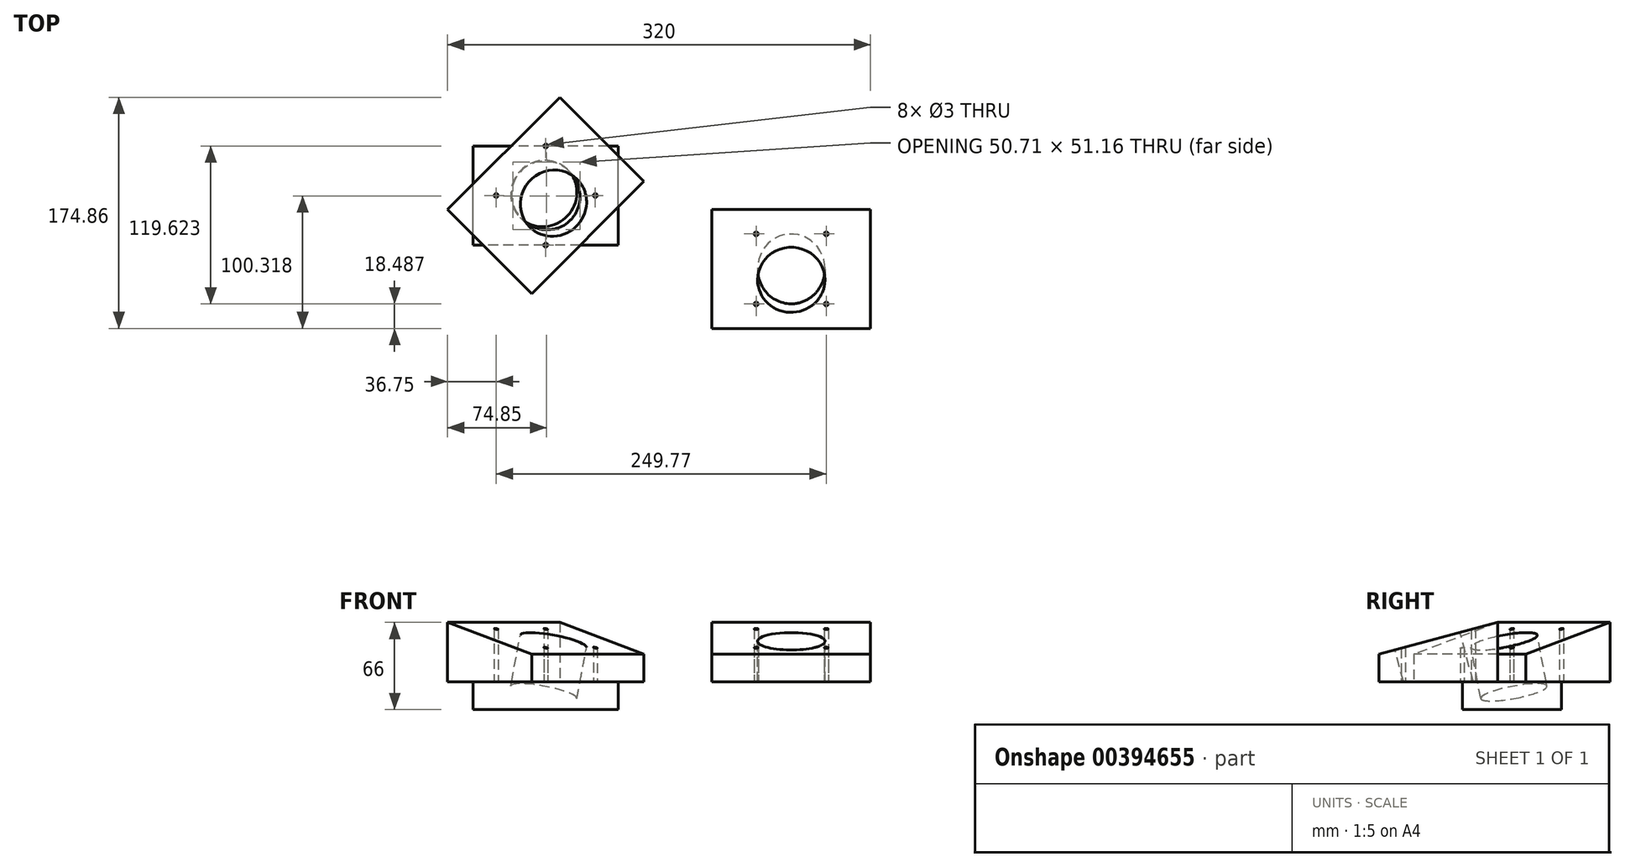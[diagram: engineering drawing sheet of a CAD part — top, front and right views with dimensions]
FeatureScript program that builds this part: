
annotation { "Feature Type Name" : "Feature", "Feature Type Description" : "" }
export const myFeature = defineFeature(function(context is Context, id is Id, definition is map)
    precondition{}
    {
        {
            var Q0;
            Q0=qCreatedBy(makeId("Top.planeOp"),FACE);
            var sketch = newSketch(context, id + "F0", { "sketchPlane" : qUnion([Q0])});
            skLineSegment(sketch, "E0.bottom", {"start": v(55, -37.5) * mm, "end": v(-55, -37.5) * mm});
            skLineSegment(sketch, "E0.top", {"start": v(55, 37.5) * mm, "end": v(-55, 37.5) * mm});
            skLineSegment(sketch, "E0.left", {"start": v(55, -37.5) * mm, "end": v(55, 37.5) * mm});
            skLineSegment(sketch, "E0.right", {"start": v(-55, -37.5) * mm, "end": v(-55, 37.5) * mm});
            skPoint(sketch, "E0.middle", {"position": v(0, 0) * mm});
            skSolve(sketch);
        }
        {
            var Q0;
            Q0=makeQuery(id+"F0.imprint","IMPRINT",FACE,{"disambiguationData":[TD([[makeQuery(id+"F0.imprint","IMPRINT",EDGE,{"derivedFrom":sQuery(id+"F0.wireOp",EDGE,"E0.bottom")}),-1.0]])]});
            extrude(context, id + "F1", {"entities" : qUnion([Q0]), "depth" : 21 * mm, "offsetDistance" : 25 * mm});
        }
        {
            var Q0;
            Q0=makeQuery(id+"F1.opExtrude","CAP_FACE",FACE,{"disambiguationData":[OSD([sQuery(id+"F0.wireOp",EDGE,"E0.bottom"),sQuery(id+"F0.wireOp",EDGE,"E0.top"),sQuery(id+"F0.wireOp",EDGE,"E0.left"),sQuery(id+"F0.wireOp",EDGE,"E0.right")])],"isStart":false});
            var sketch = newSketch(context, id + "F2", { "sketchPlane" : qUnion([Q0])});
            skLineSegment(sketch, "E1.bottom", {"start": v(74.25, 10.6) * mm, "end": v(-10.6, -74.25) * mm});
            skLineSegment(sketch, "E1.top", {"start": v(10.6, 74.25) * mm, "end": v(-74.25, -10.6) * mm});
            skLineSegment(sketch, "E1.left", {"start": v(74.25, 10.6) * mm, "end": v(10.6, 74.25) * mm});
            skLineSegment(sketch, "E1.right", {"start": v(-10.6, -74.25) * mm, "end": v(-74.25, -10.6) * mm});
            skPoint(sketch, "E1.middle", {"position": v(0, 0) * mm});
            skPoint(sketch, "E2", {"position": v(0, -37.5) * mm});
            skPoint(sketch, "E3", {"position": v(0, 37.5) * mm});
            skLineSegment(sketch, "E4", {"start": v(0, 37.5) * mm, "end": v(0, 0) * mm, "construction": true});
            skLineSegment(sketch, "E5", {"start": v(0, 0) * mm, "end": v(0, -37.5) * mm, "construction": true});
            skCircle(sketch, "E6", {"center": v(0, 0) * mm, "radius": 37.5 * mm, "construction": true});
            skPoint(sketch, "E7", {"position": v(-37.5, 0) * mm});
            skPoint(sketch, "E8", {"position": v(37.5, 0) * mm});
            skSolve(sketch);
        }
        {
            var Q0;
            {var subQ1=sQuery(id+"F0.wireOp",EDGE,"jgl5AkqR-eAGR-56ZF-mnzU-N959yiY13VDN.bottom");var subQ4=makeQuery(id+"F1.opExtrude","CAP_EDGE",EDGE,{"disambiguationData":[OSD([subQ1])],"isStart":true});var subQ14=sQuery(id+"F2.wireOp",EDGE,"UEIQAsqb-gywI-p98B-akOC-I65iesQ6cqrz");var subQ15=makeQuery(id+"F2.imprint","INTERSECT",VERTEX,{"derivedFrom":[subQ4,subQ14]});Q0=makeQuery(id+"F2.imprint","IMPRINT",FACE,{"disambiguationData":[TD([[makeQuery(id+"F2.imprint","IMPRINT",EDGE,{"disambiguationData":[TD([[subQ15,-1.0]])],"derivedFrom":subQ4}),-1.0]])]});}
            var Q1;
            {var subQ0=sQuery(id+"F2.wireOp",EDGE,"yIRzY0If-tzpD-BqDJ-z9Dj-N4k4kSrZjlb6");var subQ1=sQuery(id+"F2.wireOp",EDGE,"UEIQAsqb-gywI-p98B-akOC-I65iesQ6cqrz");var subQ2=makeQuery(id+"F2.imprint","INTERSECT",VERTEX,{"derivedFrom":[subQ1,subQ0]});Q1=makeQuery(id+"F2.imprint","IMPRINT",FACE,{"disambiguationData":[TD([[makeQuery(id+"F2.imprint","IMPRINT",EDGE,{"disambiguationData":[TD([[subQ2,-1.0]])],"derivedFrom":subQ1}),1.0]])]});}
            var Q2;
            {var subQ0=sQuery(id+"F2.wireOp",EDGE,"yIRzY0If-tzpD-BqDJ-z9Dj-N4k4kSrZjlb6");var subQ1=sQuery(id+"F2.wireOp",EDGE,"iz0sd4YI-wBiT-vDx4-GhZu-opvlAlIrHJA4");var subQ2=makeQuery(id+"F2.imprint","INTERSECT",VERTEX,{"derivedFrom":[subQ1,subQ0]});Q2=makeQuery(id+"F2.imprint","IMPRINT",FACE,{"disambiguationData":[TD([[makeQuery(id+"F2.imprint","IMPRINT",EDGE,{"disambiguationData":[TD([[subQ2,1.0]])],"derivedFrom":subQ1}),1.0]])]});}
            var Q3;
            {var subQ0=sQuery(id+"F2.wireOp",EDGE,"iz0sd4YI-wBiT-vDx4-GhZu-opvlAlIrHJA4");var subQ1=sQuery(id+"F2.wireOp",EDGE,"ij8z5wyk-LIzF-1l5R-Q5WH-tvK808gOXlXU");var subQ2=makeQuery(id+"F2.imprint","INTERSECT",VERTEX,{"derivedFrom":[subQ1,subQ0]});Q3=makeQuery(id+"F2.imprint","IMPRINT",FACE,{"disambiguationData":[TD([[makeQuery(id+"F2.imprint","IMPRINT",EDGE,{"disambiguationData":[TD([[subQ2,1.0]])],"derivedFrom":subQ1}),1.0]])]});}
            var Q4;
            {var subQ0=sQuery(id+"F2.wireOp",EDGE,"ij8z5wyk-LIzF-1l5R-Q5WH-tvK808gOXlXU");var subQ1=sQuery(id+"F2.wireOp",EDGE,"UEIQAsqb-gywI-p98B-akOC-I65iesQ6cqrz");var subQ2=makeQuery(id+"F2.imprint","INTERSECT",VERTEX,{"derivedFrom":[subQ1,subQ0]});Q4=makeQuery(id+"F2.imprint","IMPRINT",FACE,{"disambiguationData":[TD([[makeQuery(id+"F2.imprint","IMPRINT",EDGE,{"disambiguationData":[TD([[subQ2,1.0]])],"derivedFrom":subQ1}),1.0]])]});}
            var Q5;
            {var subQ0=sQuery(id+"F2.wireOp",EDGE,"E1.right");var subQ1=sQuery(id+"F2.wireOp",EDGE,"E1.top");var subQ2=makeQuery(id+"F2.imprint","INTERSECT",VERTEX,{"derivedFrom":[subQ1,subQ0]});Q5=makeQuery(id+"F2.imprint","IMPRINT",FACE,{"disambiguationData":[TD([[makeQuery(id+"F2.imprint","IMPRINT",EDGE,{"disambiguationData":[TD([[subQ2,1.0]])],"derivedFrom":subQ1}),1.0]])]});}
            var Q6;
            {var subQ6=makeQuery(id+"F1.opExtrude","CAP_EDGE",EDGE,{"disambiguationData":[OSD([sQuery(id+"F0.wireOp",EDGE,"E0.left")])],"isStart":false});var subQ13=sQuery(id+"F2.wireOp",EDGE,"E1.bottom");var subQ14=makeQuery(id+"F2.imprint","INTERSECT",VERTEX,{"derivedFrom":[subQ6,subQ13]});Q6=makeQuery(id+"F2.imprint","IMPRINT",FACE,{"disambiguationData":[TD([[makeQuery(id+"F2.imprint","IMPRINT",EDGE,{"disambiguationData":[TD([[subQ14,-1.0]])],"derivedFrom":subQ13}),-1.0]])]});}
            var Q7;
            {var subQ0=sQuery(id+"F2.wireOp",EDGE,"E1.left");var subQ1=sQuery(id+"F2.wireOp",EDGE,"E1.top");var subQ2=makeQuery(id+"F2.imprint","INTERSECT",VERTEX,{"derivedFrom":[subQ1,subQ0]});Q7=makeQuery(id+"F2.imprint","IMPRINT",FACE,{"disambiguationData":[TD([[makeQuery(id+"F2.imprint","IMPRINT",EDGE,{"disambiguationData":[TD([[subQ2,-1.0]])],"derivedFrom":subQ1}),1.0]])]});}
            var Q8;
            {var subQ0=sQuery(id+"F2.wireOp",EDGE,"E1.left");var subQ1=sQuery(id+"F2.wireOp",EDGE,"E1.bottom");var subQ2=makeQuery(id+"F2.imprint","INTERSECT",VERTEX,{"derivedFrom":[subQ1,subQ0]});Q8=makeQuery(id+"F2.imprint","IMPRINT",FACE,{"disambiguationData":[TD([[makeQuery(id+"F2.imprint","IMPRINT",EDGE,{"disambiguationData":[TD([[subQ2,-1.0]])],"derivedFrom":subQ1}),-1.0]])]});}
            var Q9;
            {var subQ0=sQuery(id+"F2.wireOp",EDGE,"E1.right");var subQ1=sQuery(id+"F2.wireOp",EDGE,"E1.bottom");var subQ2=makeQuery(id+"F2.imprint","INTERSECT",VERTEX,{"derivedFrom":[subQ1,subQ0]});Q9=makeQuery(id+"F2.imprint","IMPRINT",FACE,{"disambiguationData":[TD([[makeQuery(id+"F2.imprint","IMPRINT",EDGE,{"disambiguationData":[TD([[subQ2,1.0]])],"derivedFrom":subQ1}),-1.0]])]});}
            extrude(context, id + "F3", {"entities" : qUnion([Q0, Q1, Q2, Q3, Q4, Q5, Q6, Q7, Q8, Q9]), "depth" : 45 * mm, "offsetDistance" : 25 * mm});
        }
        {
            var Q0;
            Q0=makeQuery(id+"F3.opExtrude","SWEPT_FACE",FACE,{"disambiguationData":[OSD([sQuery(id+"F2.wireOp",EDGE,"E1.right")])]});
            var sketch = newSketch(context, id + "F4", { "sketchPlane" : qUnion([Q0])});
            skLineSegment(sketch, "E9", {"start": v(-45, 66) * mm, "end": v(45, 41.88) * mm});
            skPoint(sketch, "E10.0", {"position": v(0, 21) * mm});
            skLineSegment(sketch, "E11", {"start": v(0, 21) * mm, "end": v(8.24, 51.74) * mm, "construction": true});
            skPoint(sketch, "E12", {"position": v(8.24, 51.74) * mm});
            skSolve(sketch);
        }
        {
            var Q0;
            {var subQ0=sQuery(id+"F4.wireOp",EDGE,"E9");Q0=makeQuery(id+"F4.imprint","IMPRINT",FACE,{"disambiguationData":[TD([[makeQuery(id+"F4.imprint","IMPRINT",EDGE,{"derivedFrom":subQ0}),1.0]])]});}
            var Q1;
            Q1=makeQuery(id+"F3.opExtrude","SWEPT_FACE",FACE,{"disambiguationData":[OSD([sQuery(id+"F2.wireOp",EDGE,"E1.left")])]});
            extrude(context, id + "F5", {"entities" : qUnion([Q0]), "operationType" : NewBodyOperationType.REMOVE, "endBound" : BoundingType.UP_TO_SURFACE, "oppositeDirection" : true, "depth" : 25 * mm, "endBoundEntityFace" : qUnion([Q1]), "offsetDistance" : 25 * mm});
        }
        {
            var Q0;
            Q0=makeQuery(id+"F5.boolean.opBoolean","COPY",FACE,{"derivedFrom":makeQuery(id+"F5.opExtrude","SWEPT_FACE",FACE,{"disambiguationData":[OSD([sQuery(id+"F4.wireOp",EDGE,"E9")])]})});
            var sketch = newSketch(context, id + "F6", { "sketchPlane" : qUnion([Q0])});
            skCircle(sketch, "E13", {"center": v(-3.78, 3.9) * mm, "radius": 25.5 * mm});
            skCircle(sketch, "E14", {"center": v(-3.78, 3.9) * mm, "radius": 21 * mm});
            skLineSegment(sketch, "E15", {"start": v(-46.93, -37.78) * mm, "end": v(39.38, 45.6) * mm, "construction": true});
            skSolve(sketch);
        }
        {
            var Q0;
            Q0=makeQuery(id+"F6.imprint","IMPRINT",FACE,{"disambiguationData":[TD([[makeQuery(id+"F6.imprint","IMPRINT",EDGE,{"derivedFrom":sQuery(id+"F6.wireOp",EDGE,"E13")}),1.0]])]});
            var Q1;
            Q1=makeQuery(id+"F6.imprint","IMPRINT",FACE,{"disambiguationData":[TD([[makeQuery(id+"F6.imprint","IMPRINT",EDGE,{"derivedFrom":sQuery(id+"F6.wireOp",EDGE,"E14")}),1.0]])]});
            extrude(context, id + "F7", {"entities" : qUnion([Q0, Q1]), "operationType" : NewBodyOperationType.REMOVE, "oppositeDirection" : true, "depth" : 40 * mm, "offsetDistance" : 25 * mm});
        }
        {
            var Q0;
            Q0=sQuery(id+"F2.wireOp",VERTEX,"E7");
            var Q1;
            Q1=sQuery(id+"F2.wireOp",VERTEX,"E2");
            var Q2;
            Q2=sQuery(id+"F2.wireOp",VERTEX,"E8");
            var Q3;
            Q3=sQuery(id+"F2.wireOp",VERTEX,"E3");
            var Q4;
            Q4=makeQuery(id+"F3.opExtrude","SWEPT_BODY",BODY,{"disambiguationData":[OSD([sQuery(id+"F2.wireOp",EDGE,"E1.bottom"),sQuery(id+"F2.wireOp",EDGE,"E1.top"),sQuery(id+"F2.wireOp",EDGE,"E1.left"),sQuery(id+"F2.wireOp",EDGE,"E1.right")])]});
            hole(context, id + "F8", {"style" : HoleStyle.SIMPLE, "endStyle" : HoleEndStyle.THROUGH, "oppositeDirection" : true, "holeDiameter" : 3 * mm, "majorDiameter" : 5 * mm, "tappedDepth" : 12 * mm, "tapClearance" : 3, "startFromSketch" : true, "locations" : qUnion([Q0, Q1, Q2, Q3]), "scope" : qUnion([Q4])});
        }
        {
            var Q0;
            Q0=makeQuery(id+"F6.imprint","IMPRINT",FACE,{"disambiguationData":[TD([[makeQuery(id+"F6.imprint","IMPRINT",EDGE,{"derivedFrom":sQuery(id+"F6.wireOp",EDGE,"E14")}),1.0]])]});
            extrude(context, id + "F9", {"entities" : qUnion([Q0]), "operationType" : NewBodyOperationType.REMOVE, "oppositeDirection" : true, "depth" : 38 * mm, "offsetDistance" : 25 * mm});
        }
        {
            var Q0;
            Q0=makeQuery(id+"F3.opExtrude","SWEPT_BODY",BODY,{"disambiguationData":[OSD([sQuery(id+"F2.wireOp",EDGE,"E1.bottom"),sQuery(id+"F2.wireOp",EDGE,"E1.top"),sQuery(id+"F2.wireOp",EDGE,"E1.left"),sQuery(id+"F2.wireOp",EDGE,"E1.right")])]});
            transform(context, id + "F10", {"entities" : qUnion([Q0]), "transformType" : TransformType.TRANSLATION_3D, "dx" : 200 * mm, "dy" : 0 * mm, "dz" : 0 * mm, "makeCopy" : true});
        }
        {
            var Q0;
            Q0=makeQuery(id+"F10.opPattern","COPY",BODY,{"derivedFrom":makeQuery(id+"F3.opExtrude","SWEPT_BODY",BODY,{"disambiguationData":[OSD([sQuery(id+"F2.wireOp",EDGE,"E1.bottom"),sQuery(id+"F2.wireOp",EDGE,"E1.top"),sQuery(id+"F2.wireOp",EDGE,"E1.left"),sQuery(id+"F2.wireOp",EDGE,"E1.right")])]}),"instanceName":"1"});
            var Q1;
            Q1=makeQuery(id+"F10.opPattern","COPY",EDGE,{"derivedFrom":makeQuery(id+"F3.opExtrude","SWEPT_EDGE",EDGE,{"disambiguationData":[OSD([sQuery(id+"F2.wireOp",EDGE,"E1.top"),sQuery(id+"F2.wireOp",EDGE,"E1.right")])]}),"instanceName":"1"});
            transform(context, id + "F11", {"entities" : qUnion([Q0]), "transformType" : TransformType.ROTATION, "transformAxis" : qUnion([Q1]), "angle" : 45 * degree, "makeCopy" : false});
        }
    });
